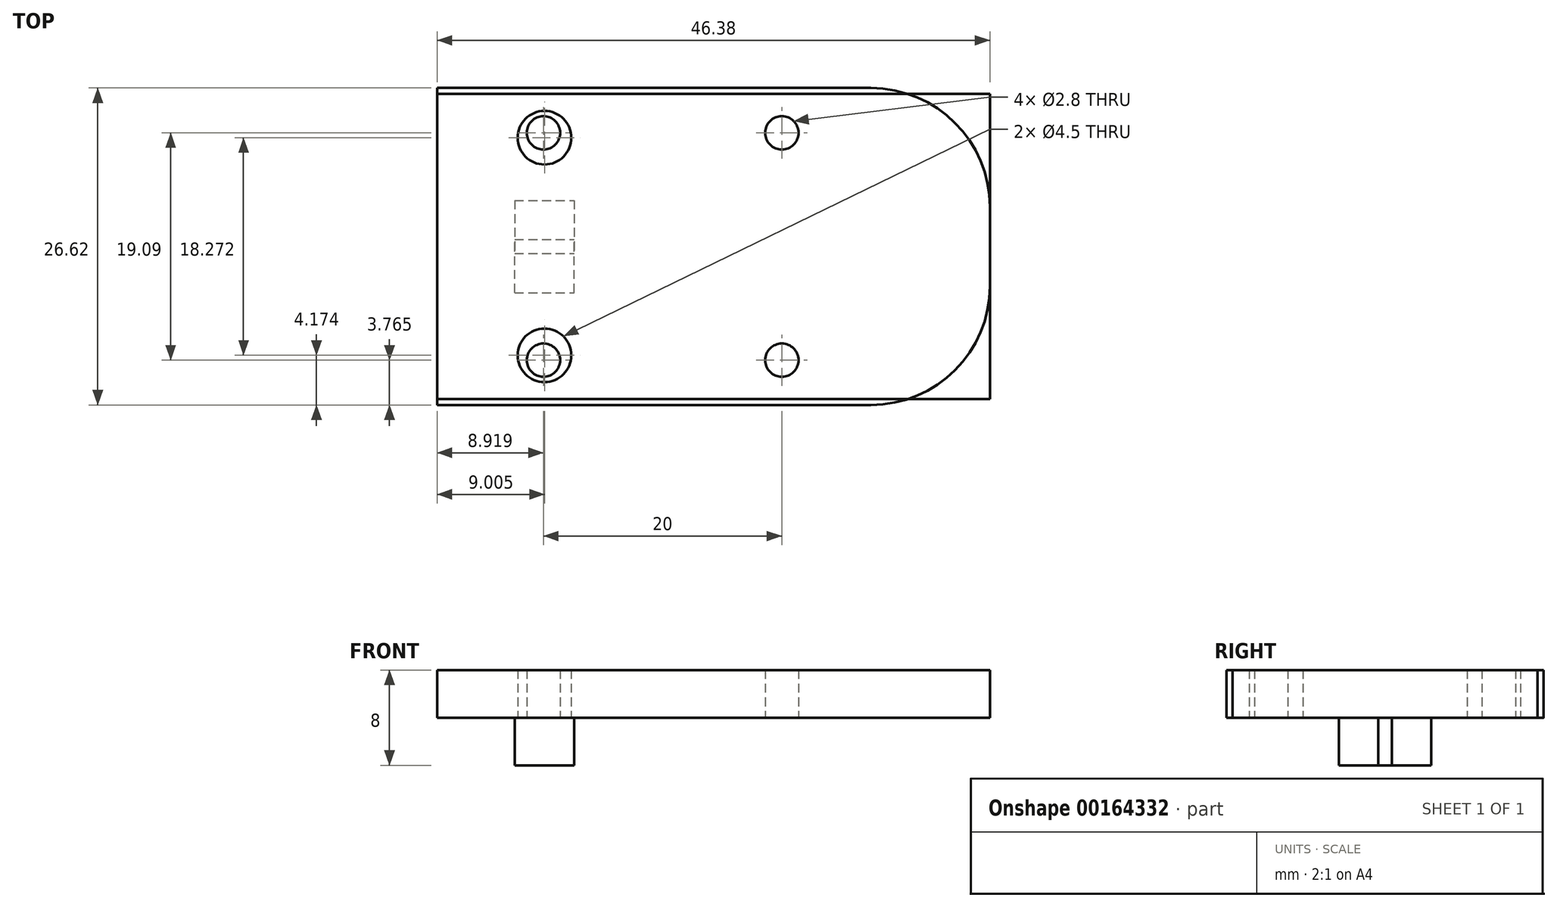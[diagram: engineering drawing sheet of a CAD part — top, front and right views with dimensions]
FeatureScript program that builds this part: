
annotation { "Feature Type Name" : "Feature", "Feature Type Description" : "" }
export const myFeature = defineFeature(function(context is Context, id is Id, definition is map)
    precondition{}
    {
        {
            var Q0;
            Q0=qCreatedBy(makeId("Top.planeOp"),FACE);
            var sketch = newSketch(context, id + "F0", { "sketchPlane" : qUnion([Q0])});
            skLineSegment(sketch, "E0.bottom", {"start": v(-43.89, 13.31) * mm, "end": v(2.5, 13.31) * mm});
            skLineSegment(sketch, "E0.top", {"start": v(-43.89, -12.8) * mm, "end": v(2.5, -12.8) * mm});
            skLineSegment(sketch, "E0.left", {"start": v(-43.89, 13.31) * mm, "end": v(-43.89, -12.8) * mm});
            skLineSegment(sketch, "E0.right", {"start": v(2.5, 13.31) * mm, "end": v(2.5, -12.8) * mm});
            skCircle(sketch, "E1", {"center": v(-34.89, 9.14) * mm, "radius": 2.25 * mm});
            skCircle(sketch, "E2", {"center": v(-34.97, -9.54) * mm, "radius": 1.4 * mm});
            skCircle(sketch, "E3", {"center": v(-14.97, -9.54) * mm, "radius": 1.4 * mm});
            skSolve(sketch);
        }
        {
            var Q0;
            Q0 = qSketchRegion(id + "F0", true);
            extrude(context, id + "F1", {"entities" : qUnion([Q0]), "depth" : 4 * mm});
        }
        {
            var Q0;
            Q0=makeQuery(id+"F1.opExtrude","CAP_FACE",FACE,{"disambiguationData":[OSD([sQuery(id+"F0.wireOp",EDGE,"E0.bottom"),sQuery(id+"F0.wireOp",EDGE,"E0.top"),sQuery(id+"F0.wireOp",EDGE,"E0.left"),sQuery(id+"F0.wireOp",EDGE,"E0.right"),sQuery(id+"F0.wireOp",EDGE,"E1"),sQuery(id+"F0.wireOp",EDGE,"E2"),sQuery(id+"F0.wireOp",EDGE,"E3")])],"isStart":true});
            var sketch = newSketch(context, id + "F2", { "sketchPlane" : qUnion([Q0])});
            skLineSegment(sketch, "E4.bottom", {"start": v(-37.39, 3.87) * mm, "end": v(-32.39, 3.87) * mm});
            skLineSegment(sketch, "E4.top", {"start": v(-37.39, -0.58) * mm, "end": v(-32.39, -0.58) * mm});
            skLineSegment(sketch, "E4.left", {"start": v(-37.39, 3.87) * mm, "end": v(-37.39, -0.58) * mm});
            skLineSegment(sketch, "E4.right", {"start": v(-32.39, 3.87) * mm, "end": v(-32.39, -0.58) * mm});
            skLineSegment(sketch, "E5", {"start": v(-34.89, -9.14) * mm, "end": v(-34.89, 5.1) * mm, "construction": true});
            skSolve(sketch);
        }
        {
            var Q0;
            Q0 = qSketchRegion(id + "F2", true);
            extrude(context, id + "F3", {"entities" : qUnion([Q0]), "operationType" : NewBodyOperationType.ADD, "depth" : 4 * mm});
        }
        {
            var Q0;
            Q0=makeQuery(id+"F1.opExtrude","SWEPT_EDGE",EDGE,{"disambiguationData":[OSD([sQuery(id+"F0.wireOp",EDGE,"E0.bottom"),sQuery(id+"F0.wireOp",EDGE,"E0.right")])]});
            fillet(context, id + "F4", {"entities" : qUnion([Q0]), "radius" : 10 * mm, "tangentPropagation" : true, "allowEdgeOverflow" : false});
        }
        {
            var Q0;
            Q0=makeQuery(id+"F1.opExtrude","SWEPT_BODY",BODY,{"disambiguationData":[OSD([sQuery(id+"F0.wireOp",EDGE,"E0.bottom"),sQuery(id+"F0.wireOp",EDGE,"E0.top"),sQuery(id+"F0.wireOp",EDGE,"E0.left"),sQuery(id+"F0.wireOp",EDGE,"E0.right"),sQuery(id+"F0.wireOp",EDGE,"E1"),sQuery(id+"F0.wireOp",EDGE,"E2"),sQuery(id+"F0.wireOp",EDGE,"E3")])]});
            var Q1;
            Q1=qCreatedBy(makeId("Front.planeOp"),FACE);
            mirror(context, id + "F5", {"entities" : qUnion([Q0]), "mirrorPlane" : qUnion([Q1])});
        }
    });
